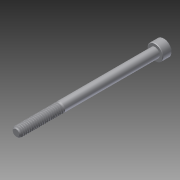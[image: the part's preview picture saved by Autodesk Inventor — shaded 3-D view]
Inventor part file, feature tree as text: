
AUTODESK INVENTOR PART (.ipt)
format: ipt  version: 2014 SP1 (Build 180222100, 222)  size: 523,264 bytes
history: native  units: in
note: dims shown in document units (in); Inventor stores cm internally (conversion verified against a paired STEP export)
features: chamfer x1, other x1, imported_body x1
ambient origin geometry x8: Origin, YZ Plane, XZ Plane, XY Plane, X Axis, Y Axis, Z Axis, Center Point
bodies: Body1 (feature_tree)
feature tree (3):
  chamfer  "Chamfer2"  [1 undecoded]
  other  "91251A2561"
  imported_body  "Base1"
note: 1 required parameter value undecoded (feature->parameter linkage not recoverable at this tier; creation-order binding heuristic only, values carry confidence <= 0.55)
